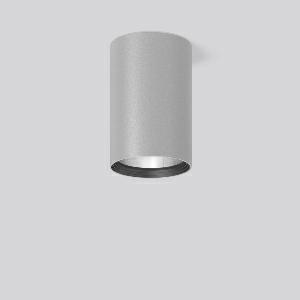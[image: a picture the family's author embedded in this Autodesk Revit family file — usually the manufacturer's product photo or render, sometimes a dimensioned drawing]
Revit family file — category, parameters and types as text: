
# Revit family: heledon_maxi_a_931226_004_3_3e18
name_source: partatom
category: Lighting Fixtures
units: mm (PartAtom-declared; Revit-internal decimal feet)

## family parameters
Cut with Voids When Loaded = No
Host = Face
Light Source = No
Part Type = Normal
Room Calculation Point = No
Round Connector Dimension = Use Diameter
Shared = No

## types (1)
- HELEDON maxi A (1 x LED Modul 935, 4200 lm, 3500)
    Apparent Load = 35 VA
    Approval mark = CE
    CIE Flux Codes = 97 100 100 100 100
    Color Rendering = 92
    Color Temperature = 3500
    Default Elevation = 1800 mm
    Description = Series: HELEDON maxi
Cylindrical surface-mounted downlight. Housing: die-cast aluminium, powder-coated. Internal ceiling frame polycarbonate with bayonet mounting. Black plastic ring and recessed LED to prevent glare from the side. Optical assembly with reflector made of MIRO-Silver with 98% total light reflection for outstanding efficiency - can be changed without tools. Best colour rendering index Ra>90. Suitable for Ceiling mounting. Easy installation with a separate ceiling frame with bayonet mounting and plug connection. Driver integrated. Connected via plug-in connector. High quality converter without flickering and stroboscopic effect. The following accessories can be mounted without use of tools: interchangeable lenses, decorative glasses, honeycomb louvre, clear and frosted diffusers, white interchangeable plastic ring. 
Colour: silver
Diameter: 123 mm
Height: 183 mm
Lamp: LED
Socket: without socket
Colour temperature: 3500K
Colour rendering index (CRI): 92
System power: 35 W
Rated luminous flux: 4200 lm
Luminous efficiency: 120 lm/W
Control gear: Regulated power supply
Protection class: I
Type of protection: IP 20
    Height = 183 mm
    Lamp = 1 x LED Modul 935
    Lamp Light Flux = 4200 lm
    Lamp count = 1
    Length = 123 mm
    Lifetime = 50000 h
    Luminous efficacy = 120 lm/W
    Manufacturer = RZB
    ModVariant = No
    Model = 931226.004.3
    Mounting Place = Ceiling
    Mounting Type = Surface mounted
    Number of Poles = 1
    OnlyDefault = Yes
    Power Factor = 1
    Product Name = HELEDON maxi A
    Product group = Surface mounted downlights
    ProductGroupID = 302
    Protection Class = Protection class I
    Protection Degree = IP 20
    RLX_Detail_Level = 1
    RLX_Emergency_Light_Flux = 0 lm
    RLX_Emergency_Type = 0
    RLX_Emergency_Type_DB = No
    RlxData = <blob elided: 98949 chars, md5=67d4470d>
    Socket = socket
    Standby Power = 0 W
    System Light Flux = 4200 lm
    System Power = 35 W
    Type Comments = Product without accessories
    Type Image = 931192.004.jpg
    URL = http://relux.com
    VarID = ---
    Voltage = 230 V
    Voltage Range = 220-240 V
    Weight = 0.00 kg
    Width = 0 mm  [stored 0 ft]

note: [stored X ft] marks values corroborated as IEEE doubles in the binary element streams (Revit-internal decimal feet)

## geometry (parser evidence)
native form markers: Blend x4, Sweep x11
no freeform markers — native parametric forms only
